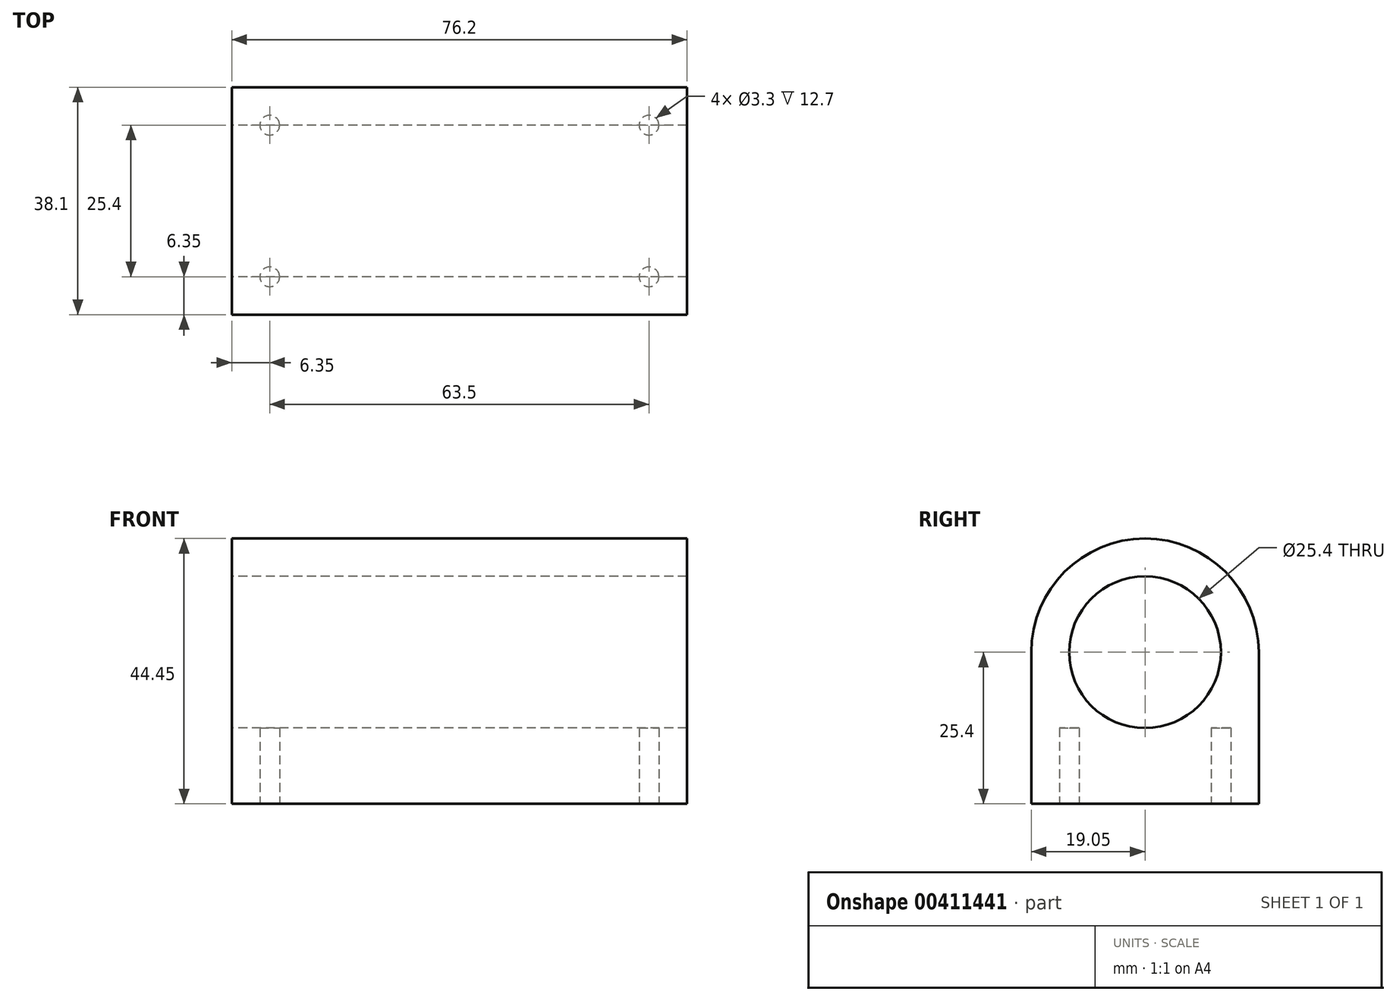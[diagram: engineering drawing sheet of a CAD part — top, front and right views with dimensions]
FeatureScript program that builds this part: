
annotation { "Feature Type Name" : "Feature", "Feature Type Description" : "" }
export const myFeature = defineFeature(function(context is Context, id is Id, definition is map)
    precondition{}
    {
        {
            var Q0;
            Q0=qCreatedBy(makeId("Right.planeOp"),FACE);
            var sketch = newSketch(context, id + "F0", { "sketchPlane" : qUnion([Q0])});
            skLineSegment(sketch, "E0", {"start": v(-19.05, 0) * mm, "end": v(-19.05, -25.4) * mm});
            skLineSegment(sketch, "E1", {"start": v(-19.05, -25.4) * mm, "end": v(19.05, -25.4) * mm});
            skLineSegment(sketch, "E2", {"start": v(19.05, -25.4) * mm, "end": v(19.05, 0) * mm});
            skArc(sketch, "E3", {"start": v(19.05, 0) * mm, "mid": v(0, 19.05) * mm, "end": v(-19.05, 0) * mm});
            skCircle(sketch, "E4", {"center": v(0, 0) * mm, "radius": 12.7 * mm});
            skSolve(sketch);
        }
        {
            var Q0;
            Q0=qSketchRegion(id+"F0",true);
            extrude(context, id + "F1", {"entities" : qUnion([Q0]), "endBound" : BoundingType.SYMMETRIC, "depth" : 76.2 * mm});
        }
        {
            var Q0;
            Q0=makeQuery(id+"F1.opExtrude","SWEPT_FACE",FACE,{"disambiguationData":[OSD([sQuery(id+"F0.wireOp",EDGE,"E1")])]});
            var sketch = newSketch(context, id + "F2", { "sketchPlane" : qUnion([Q0])});
            skCircle(sketch, "E5", {"center": v(-31.75, 12.7) * mm, "radius": 1.65 * mm});
            skCircle(sketch, "E6", {"center": v(-31.75, -12.7) * mm, "radius": 1.65 * mm});
            skCircle(sketch, "E7", {"center": v(31.75, 12.7) * mm, "radius": 1.65 * mm});
            skCircle(sketch, "E8", {"center": v(31.75, -12.7) * mm, "radius": 1.65 * mm});
            skSolve(sketch);
        }
        {
            var Q0;
            Q0=qSketchRegion(id+"F2",true);
            extrude(context, id + "F3", {"entities" : qUnion([Q0]), "operationType" : NewBodyOperationType.REMOVE, "oppositeDirection" : true, "depth" : 12.7 * mm});
        }
    });
